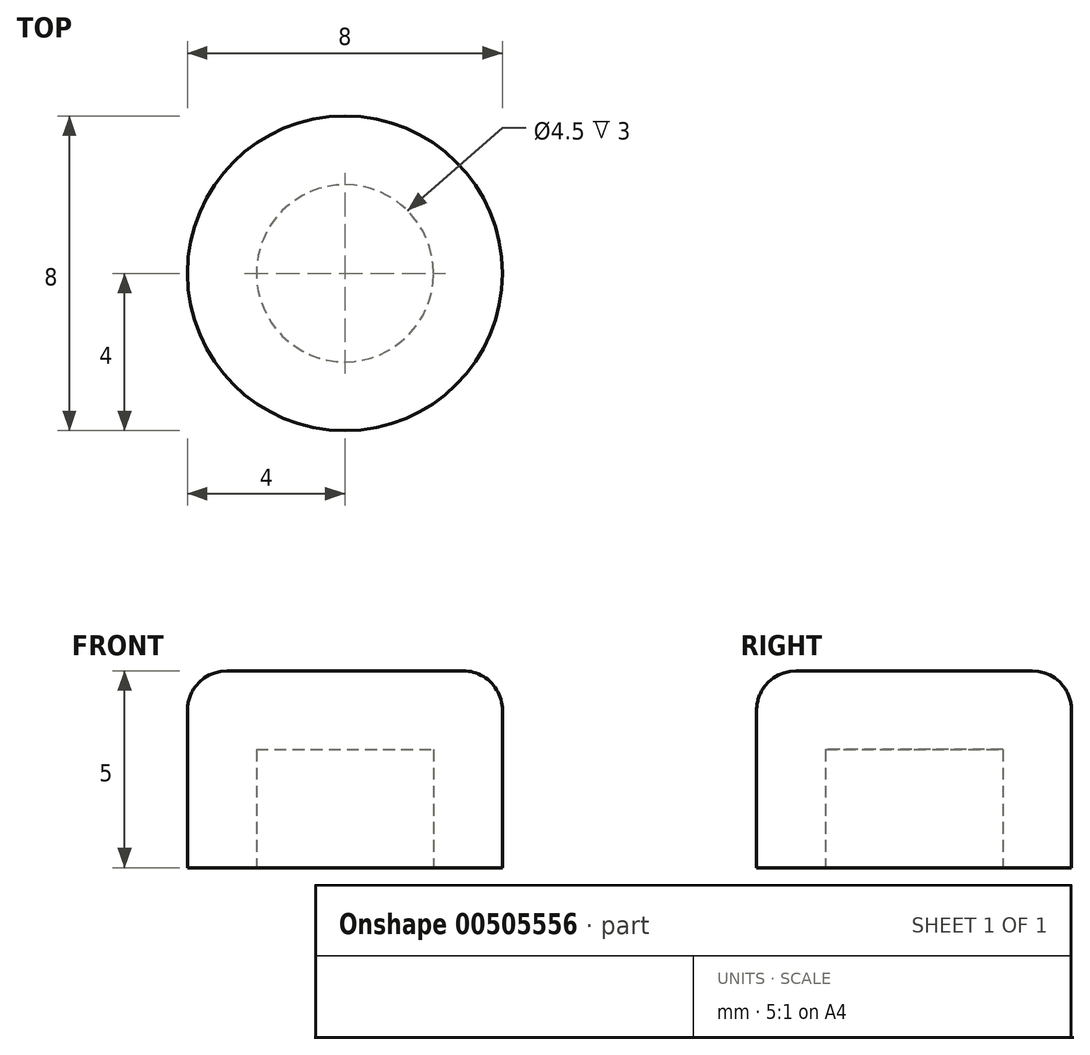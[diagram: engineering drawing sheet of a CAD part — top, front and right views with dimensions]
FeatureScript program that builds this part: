
annotation { "Feature Type Name" : "Feature", "Feature Type Description" : "" }
export const myFeature = defineFeature(function(context is Context, id is Id, definition is map)
    precondition{}
    {
        {
            var Q0;
            Q0=qCreatedBy(makeId("Top.planeOp"),FACE);
            var sketch = newSketch(context, id + "F0", { "sketchPlane" : qUnion([Q0])});
            skCircle(sketch, "E0", {"center": v(0, 0) * mm, "radius": 4 * mm});
            skSolve(sketch);
        }
        {
            var Q0;
            Q0=makeQuery(id+"F0.imprint","IMPRINT",FACE,{"disambiguationData":[TD([[makeQuery(id+"F0.imprint","IMPRINT",EDGE,{"derivedFrom":sQuery(id+"F0.wireOp",EDGE,"E0")}),1.0]])]});
            extrude(context, id + "F1", {"entities" : qUnion([Q0]), "depth" : 5 * mm});
        }
        {
            var Q0;
            Q0=makeQuery(id+"F1.opExtrude","CAP_EDGE",EDGE,{"disambiguationData":[OSD([sQuery(id+"F0.wireOp",EDGE,"E0")])],"isStart":false});
            fillet(context, id + "F2", {"entities" : qUnion([Q0]), "radius" : 1 * mm, "tangentPropagation" : true, "allowEdgeOverflow" : false});
        }
        {
            var Q0;
            Q0=makeQuery(id+"F1.opExtrude","CAP_FACE",FACE,{"disambiguationData":[OSD([sQuery(id+"F0.wireOp",EDGE,"E0")])],"isStart":true});
            var sketch = newSketch(context, id + "F3", { "sketchPlane" : qUnion([Q0])});
            skCircle(sketch, "E1", {"center": v(0, 0) * mm, "radius": 2.25 * mm});
            skSolve(sketch);
        }
        {
            var Q0;
            Q0=makeQuery(id+"F3.imprint","IMPRINT",FACE,{"disambiguationData":[TD([[makeQuery(id+"F3.imprint","IMPRINT",EDGE,{"derivedFrom":sQuery(id+"F3.wireOp",EDGE,"E1")}),1.0]])]});
            extrude(context, id + "F4", {"entities" : qUnion([Q0]), "operationType" : NewBodyOperationType.REMOVE, "oppositeDirection" : true, "depth" : 3 * mm});
        }
    });
